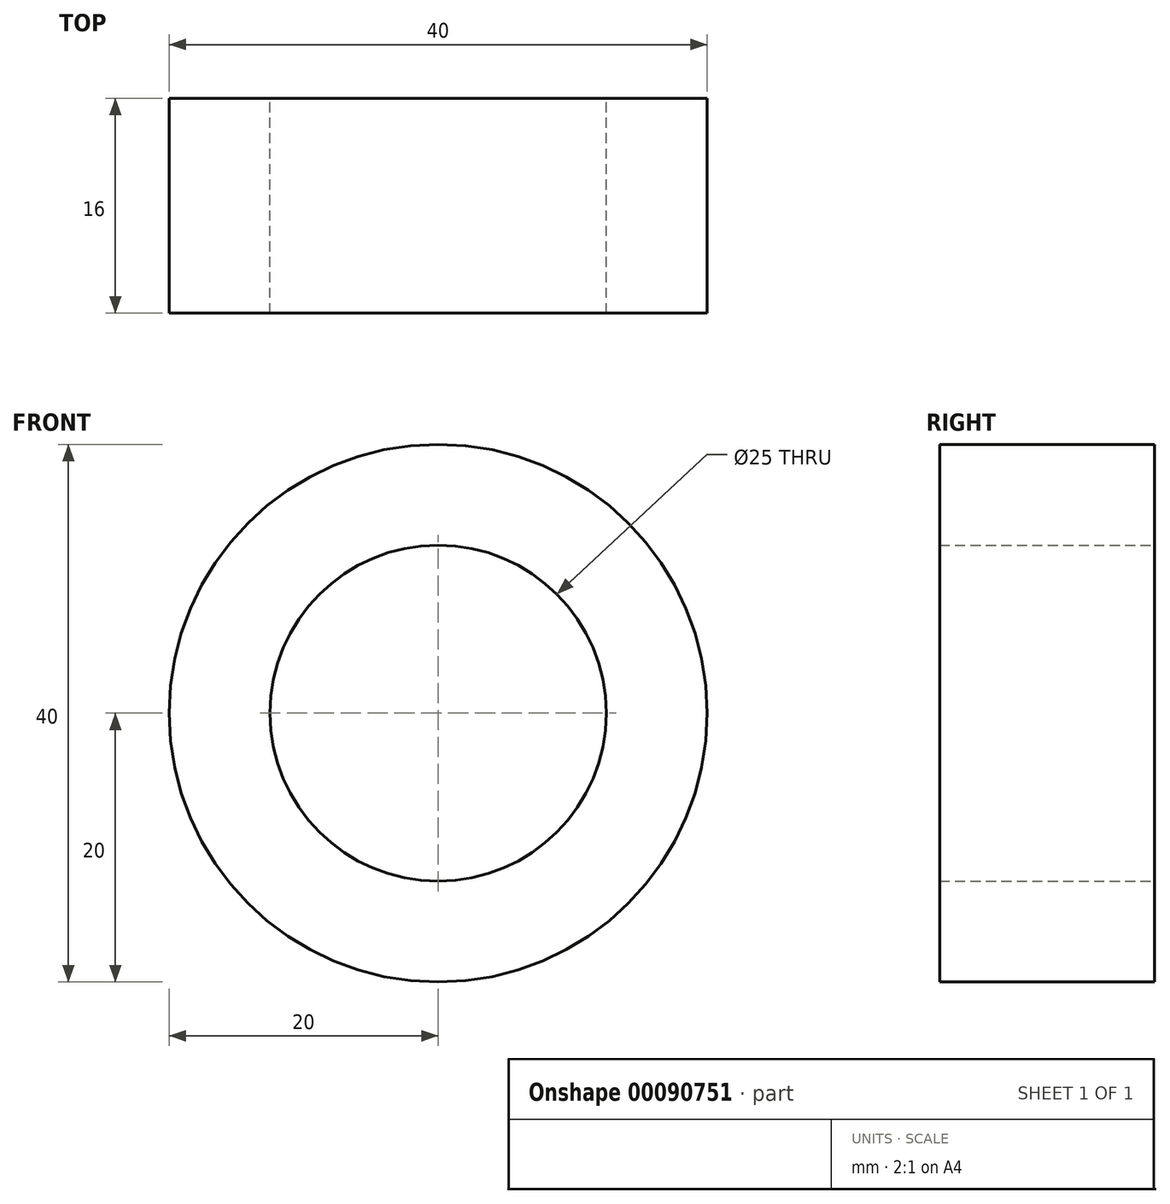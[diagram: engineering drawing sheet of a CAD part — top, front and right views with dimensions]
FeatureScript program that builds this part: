
annotation { "Feature Type Name" : "Feature", "Feature Type Description" : "" }
export const myFeature = defineFeature(function(context is Context, id is Id, definition is map)
    precondition{}
    {
        {
            var Q0;
            Q0=qCreatedBy(makeId("Front.planeOp"),FACE);
            var sketch = newSketch(context, id + "F0", { "sketchPlane" : qUnion([Q0])});
            skCircle(sketch, "E0", {"center": v(0, 0) * mm, "radius": 12.5 * mm});
            skCircle(sketch, "E1", {"center": v(0, 0) * mm, "radius": 20 * mm});
            skSolve(sketch);
        }
        {
            var Q0;
            Q0=makeQuery(id+"F0.imprint","IMPRINT",FACE,{"disambiguationData":[TD([[makeQuery(id+"F0.imprint","IMPRINT",EDGE,{"derivedFrom":sQuery(id+"F0.wireOp",EDGE,"E0")}),-1.0]])]});
            extrude(context, id + "F1", {"entities" : qUnion([Q0]), "depth" : 16 * mm});
        }
    });
